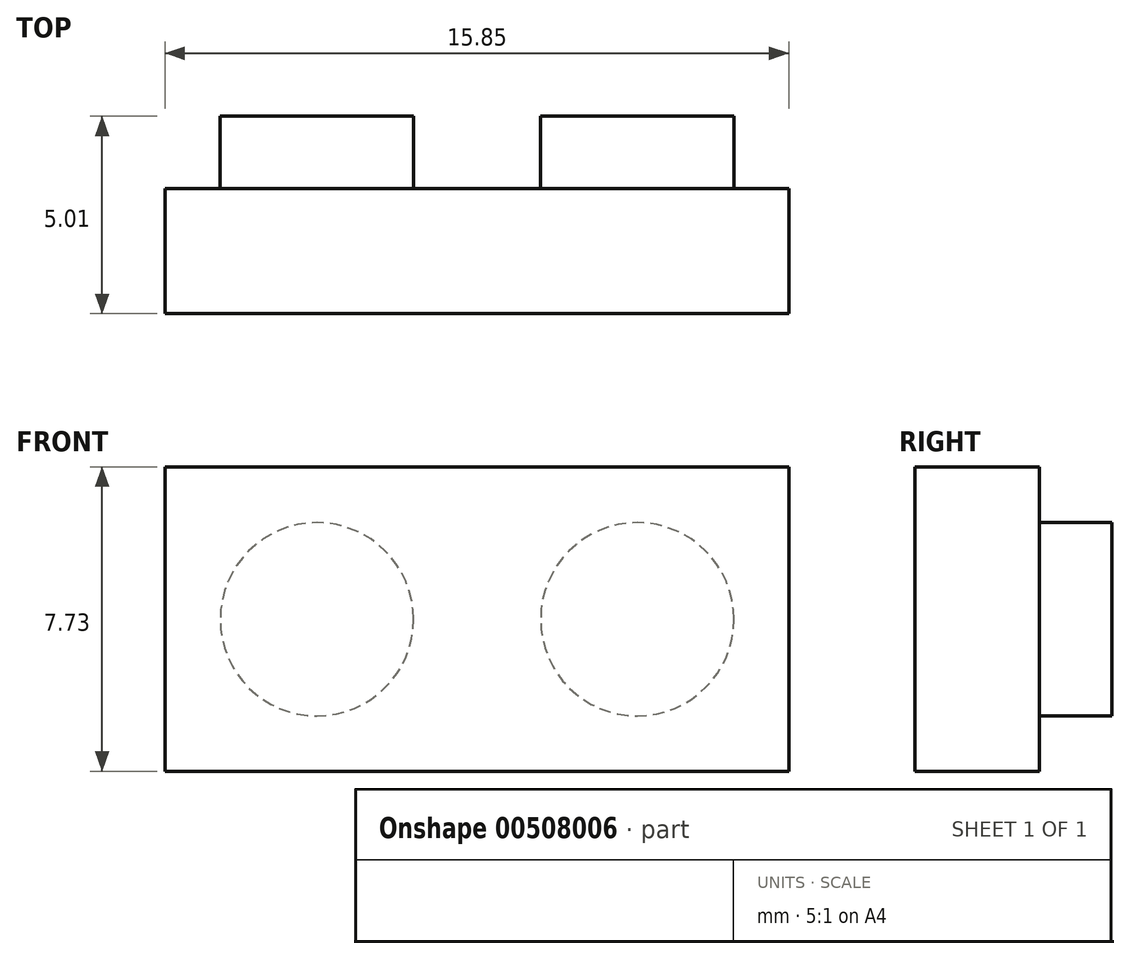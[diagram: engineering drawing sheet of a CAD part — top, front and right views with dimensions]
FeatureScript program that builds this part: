
annotation { "Feature Type Name" : "Feature", "Feature Type Description" : "" }
export const myFeature = defineFeature(function(context is Context, id is Id, definition is map)
    precondition{}
    {
        {
            var Q0;
            Q0=qCreatedBy(makeId("Front.planeOp"),FACE);
            var sketch = newSketch(context, id + "F0", { "sketchPlane" : qUnion([Q0])});
            skLineSegment(sketch, "E0.bottom", {"start": v(0, 0) * mm, "end": v(-15.85, 0) * mm});
            skLineSegment(sketch, "E0.top", {"start": v(0, 7.73) * mm, "end": v(-15.85, 7.73) * mm});
            skLineSegment(sketch, "E0.left", {"start": v(0, 0) * mm, "end": v(0, 7.73) * mm});
            skLineSegment(sketch, "E0.right", {"start": v(-15.85, 0) * mm, "end": v(-15.85, 7.73) * mm});
            skSolve(sketch);
        }
        {
            var Q0;
            Q0=makeQuery(id+"F0.imprint","IMPRINT",FACE,{"disambiguationData":[TD([[makeQuery(id+"F0.imprint","IMPRINT",EDGE,{"derivedFrom":sQuery(id+"F0.wireOp",EDGE,"E0.bottom")}),-1.0]])]});
            extrude(context, id + "F1", {"entities" : qUnion([Q0]), "depth" : 3.17 * mm, "offsetDistance" : 25 * mm});
        }
        {
            var Q0;
            Q0=qCreatedBy(makeId("Front.planeOp"),FACE);
            var sketch = newSketch(context, id + "F2", { "sketchPlane" : qUnion([Q0])});
            skCircle(sketch, "E1", {"center": v(-12, 3.86) * mm, "radius": 2.46 * mm});
            skCircle(sketch, "E2", {"center": v(-3.85, 3.86) * mm, "radius": 2.46 * mm});
            skSolve(sketch);
        }
        {
            var Q0;
            Q0=makeQuery(id+"F2.imprint","IMPRINT",FACE,{"disambiguationData":[TD([[makeQuery(id+"F2.imprint","IMPRINT",EDGE,{"derivedFrom":sQuery(id+"F2.wireOp",EDGE,"E1")}),1.0]])]});
            var Q1;
            Q1=makeQuery(id+"F2.imprint","IMPRINT",FACE,{"disambiguationData":[TD([[makeQuery(id+"F2.imprint","IMPRINT",EDGE,{"derivedFrom":sQuery(id+"F2.wireOp",EDGE,"E2")}),1.0]])]});
            extrude(context, id + "F3", {"entities" : qUnion([Q0, Q1]), "operationType" : NewBodyOperationType.ADD, "oppositeDirection" : true, "depth" : 1.84 * mm, "offsetDistance" : 25 * mm});
        }
    });
